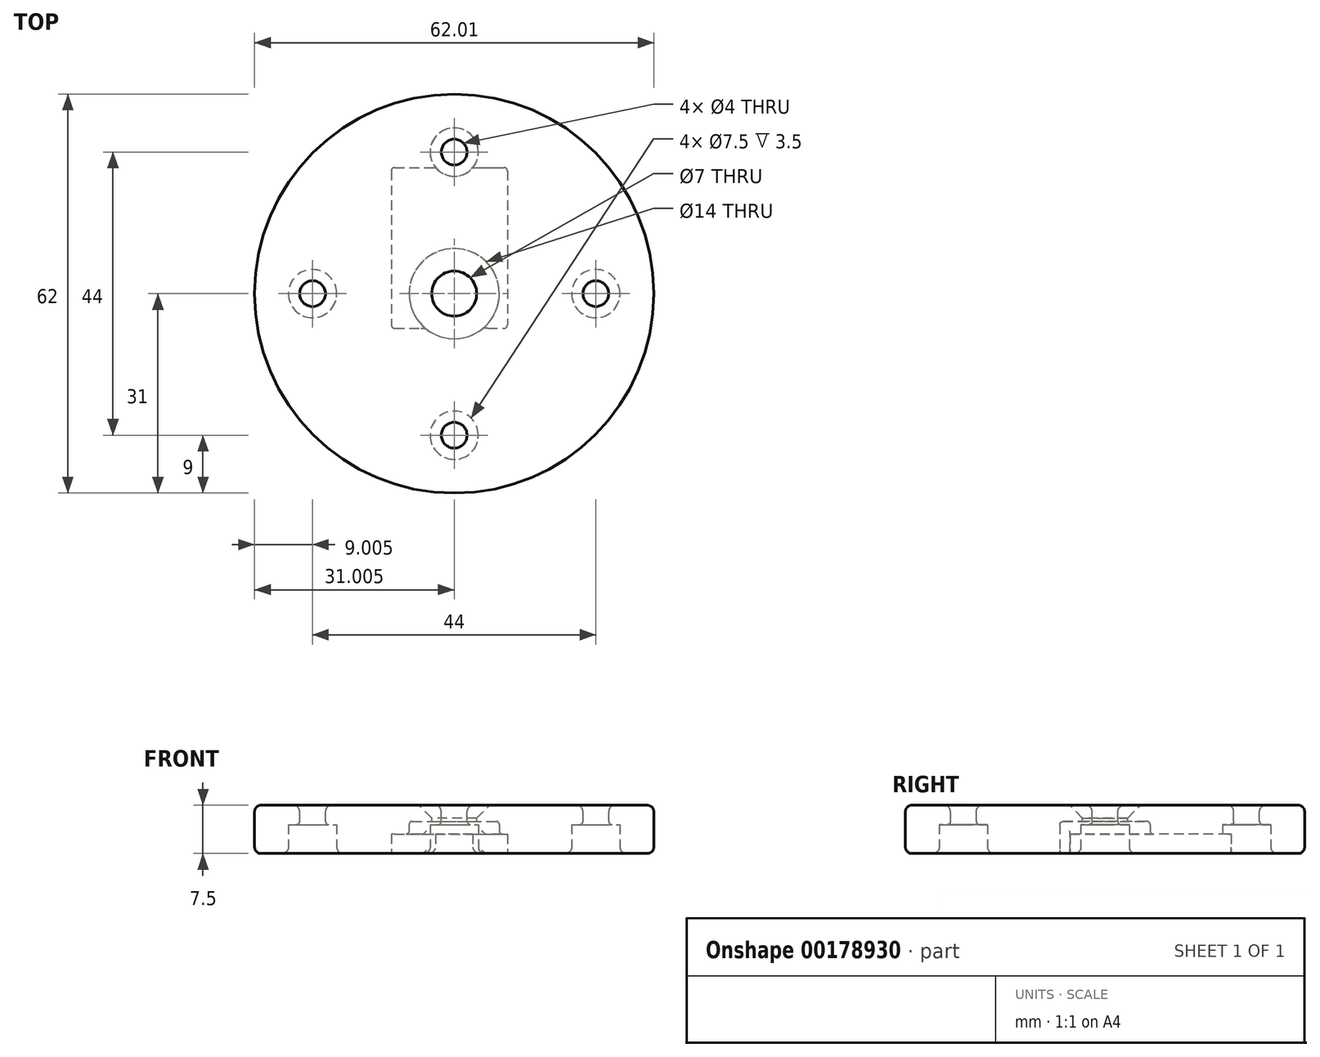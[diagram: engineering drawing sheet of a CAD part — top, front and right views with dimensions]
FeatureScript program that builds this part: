
annotation { "Feature Type Name" : "Feature", "Feature Type Description" : "" }
export const myFeature = defineFeature(function(context is Context, id is Id, definition is map)
    precondition{}
    {
        {
            var Q0;
            Q0=qCreatedBy(makeId("Top.planeOp"),FACE);
            var sketch = newSketch(context, id + "F0", { "sketchPlane" : qUnion([Q0])});
            skLineSegment(sketch, "E0", {"start": v(0, 0) * mm, "end": v(44.88, 0) * mm, "construction": true});
            skLineSegment(sketch, "E1", {"start": v(0, 0) * mm, "end": v(-44.88, 0) * mm, "construction": true});
            skCircle(sketch, "E2", {"center": v(-44.88, 0) * mm, "radius": 3.5 * mm});
            skCircle(sketch, "E3", {"center": v(44.88, 0) * mm, "radius": 3.5 * mm});
            skCircle(sketch, "E4", {"center": v(-44.88, 0) * mm, "radius": 31 * mm});
            skCircle(sketch, "E5", {"center": v(-44.88, 0) * mm, "radius": 22 * mm, "construction": true});
            skPoint(sketch, "E6", {"position": v(-44.88, 22) * mm});
            skPoint(sketch, "E7", {"position": v(-66.87, 0) * mm});
            skPoint(sketch, "E8", {"position": v(-44.88, -22) * mm});
            skPoint(sketch, "E9", {"position": v(-22.88, 0) * mm});
            skCircle(sketch, "E10", {"center": v(-44.88, 22) * mm, "radius": 2 * mm});
            skCircle(sketch, "E11", {"center": v(-66.87, 0) * mm, "radius": 2 * mm});
            skCircle(sketch, "E12", {"center": v(-44.88, -22) * mm, "radius": 2 * mm});
            skCircle(sketch, "E13", {"center": v(-22.88, 0) * mm, "radius": 2 * mm});
            skSolve(sketch);
        }
        {
            var Q0;
            Q0=makeQuery(id+"F0.imprint","IMPRINT",FACE,{"disambiguationData":[TD([[makeQuery(id+"F0.imprint","IMPRINT",EDGE,{"derivedFrom":sQuery(id+"F0.wireOp",EDGE,"E10")}),-1.0]])]});
            var Q1;
            Q1=makeQuery(id+"F0.imprint","IMPRINT",FACE,{"disambiguationData":[TD([[makeQuery(id+"F0.imprint","IMPRINT",EDGE,{"derivedFrom":sQuery(id+"F0.wireOp",EDGE,"E13")}),-1.0]])]});
            extrude(context, id + "F1", {"entities" : qUnion([Q0, Q1]), "oppositeDirection" : true, "depth" : 7.5 * mm});
        }
        {
            var Q0;
            Q0=makeQuery(id+"F1.opExtrude","CAP_FACE",FACE,{"disambiguationData":[OSD([sQuery(id+"F0.wireOp",EDGE,"UtSojWLK-Axtw-wVSr-lVTc-6Qd8189fFZQg"),sQuery(id+"F0.wireOp",EDGE,"E2"),sQuery(id+"F0.wireOp",EDGE,"E3"),sQuery(id+"F0.wireOp",EDGE,"FokHbOu8-fEOc-FsWC-vcUf-28nsGhh90SPb"),sQuery(id+"F0.wireOp",EDGE,"ryVjNOqA-lODm-GvTz-wMqV-SOG7XD1yc1lL"),sQuery(id+"F0.wireOp",EDGE,"E4"),sQuery(id+"F0.wireOp",EDGE,"E10"),sQuery(id+"F0.wireOp",EDGE,"E11"),sQuery(id+"F0.wireOp",EDGE,"E12"),sQuery(id+"F0.wireOp",EDGE,"E13")])],"isStart":false});
            var sketch = newSketch(context, id + "F2", { "sketchPlane" : qUnion([Q0])});
            skCircle(sketch, "E14", {"center": v(-44.88, 22) * mm, "radius": 3.75 * mm});
            skCircle(sketch, "E15", {"center": v(-22.88, 0) * mm, "radius": 3.75 * mm});
            skCircle(sketch, "E16", {"center": v(-44.88, -22) * mm, "radius": 3.75 * mm});
            skCircle(sketch, "E17", {"center": v(-66.87, 0) * mm, "radius": 3.75 * mm});
            skSolve(sketch);
        }
        {
            var Q0;
            Q0=qSketchRegion(id+"F2",true);
            extrude(context, id + "F3", {"entities" : qUnion([Q0]), "operationType" : NewBodyOperationType.REMOVE, "oppositeDirection" : true, "depth" : 4.5 * mm});
        }
        {
            var Q0;
            Q0=makeQuery(id+"F1.opExtrude","CAP_EDGE",EDGE,{"disambiguationData":[OSD([sQuery(id+"F0.wireOp",EDGE,"E2")])],"isStart":true});
            chamfer(context, id + "F4", {"entities" : qUnion([Q0]), "width" : 2 * mm, "tangentPropagation" : true});
        }
        {
            var Q0;
            Q0=makeQuery(id+"FrYEty1sIvLQoTp_1.opExtrude","CAP_FACE",FACE,{"disambiguationData":[OSD([sQuery(id+"F0.wireOp",EDGE,"S2UXTJ5L-PYoN-hTdS-oQlw-xzllwW9uqox5"),sQuery(id+"F0.wireOp",EDGE,"E2")])],"isStart":false});
            var Q1;
            Q1=makeQuery(id+"F1.opExtrude","CAP_FACE",FACE,{"disambiguationData":[OSD([sQuery(id+"F0.wireOp",EDGE,"S2UXTJ5L-PYoN-hTdS-oQlw-xzllwW9uqox5"),sQuery(id+"F0.wireOp",EDGE,"UtSojWLK-Axtw-wVSr-lVTc-6Qd8189fFZQg"),sQuery(id+"F0.wireOp",EDGE,"E2"),sQuery(id+"F0.wireOp",EDGE,"E3"),sQuery(id+"F0.wireOp",EDGE,"FokHbOu8-fEOc-FsWC-vcUf-28nsGhh90SPb"),sQuery(id+"F0.wireOp",EDGE,"ryVjNOqA-lODm-GvTz-wMqV-SOG7XD1yc1lL")])],"isStart":true});
            var Q2;
            Q2=makeQuery(id+"FrYEty1sIvLQoTp_1.opExtrude","CAP_FACE",FACE,{"disambiguationData":[OSD([sQuery(id+"F0.wireOp",EDGE,"UtSojWLK-Axtw-wVSr-lVTc-6Qd8189fFZQg"),sQuery(id+"F0.wireOp",EDGE,"E3")])],"isStart":false});
            var Q3;
            Q3=makeQuery(id+"F1.opExtrude","CAP_FACE",FACE,{"disambiguationData":[OSD([sQuery(id+"F0.wireOp",EDGE,"S2UXTJ5L-PYoN-hTdS-oQlw-xzllwW9uqox5"),sQuery(id+"F0.wireOp",EDGE,"UtSojWLK-Axtw-wVSr-lVTc-6Qd8189fFZQg"),sQuery(id+"F0.wireOp",EDGE,"E2"),sQuery(id+"F0.wireOp",EDGE,"E3"),sQuery(id+"F0.wireOp",EDGE,"FokHbOu8-fEOc-FsWC-vcUf-28nsGhh90SPb"),sQuery(id+"F0.wireOp",EDGE,"ryVjNOqA-lODm-GvTz-wMqV-SOG7XD1yc1lL")])],"isStart":false});
            fillet(context, id + "F5", {"entities" : qUnion([Q0, Q1, Q2, Q3]), "radius" : 1 * mm, "tangentPropagation" : true, "allowEdgeOverflow" : false});
        }
        {
            var Q0;
            Q0=makeQuery(id+"F1.opExtrude","SWEPT_FACE",FACE,{"disambiguationData":[OSD([sQuery(id+"F0.wireOp",EDGE,"E11")])]});
            var Q1;
            Q1=makeQuery(id+"F1.opExtrude","SWEPT_FACE",FACE,{"disambiguationData":[OSD([sQuery(id+"F0.wireOp",EDGE,"E12")])]});
            var Q2;
            Q2=makeQuery(id+"F1.opExtrude","SWEPT_FACE",FACE,{"disambiguationData":[OSD([sQuery(id+"F0.wireOp",EDGE,"E13")])]});
            var Q3;
            Q3=makeQuery(id+"F1.opExtrude","SWEPT_FACE",FACE,{"disambiguationData":[OSD([sQuery(id+"F0.wireOp",EDGE,"E10")])]});
            fillet(context, id + "F6", {"entities" : qUnion([Q0, Q1, Q2, Q3]), "radius" : .5 * mm, "tangentPropagation" : true, "allowEdgeOverflow" : false});
        }
        {
            var Q0;
            Q0=makeQuery(id+"F1.opExtrude","CAP_FACE",FACE,{"disambiguationData":[OSD([sQuery(id+"F0.wireOp",EDGE,"E2"),sQuery(id+"F0.wireOp",EDGE,"E4"),sQuery(id+"F0.wireOp",EDGE,"E10"),sQuery(id+"F0.wireOp",EDGE,"E11"),sQuery(id+"F0.wireOp",EDGE,"E12"),sQuery(id+"F0.wireOp",EDGE,"E13")])],"isStart":false});
            var sketch = newSketch(context, id + "F7", { "sketchPlane" : qUnion([Q0])});
            skLineSegment(sketch, "E18.bottom", {"start": v(-54.62, -19.6) * mm, "end": v(-36.62, -19.6) * mm});
            skLineSegment(sketch, "E18.top", {"start": v(-54.62, 5.4) * mm, "end": v(-36.62, 5.4) * mm});
            skLineSegment(sketch, "E18.left", {"start": v(-54.62, -19.6) * mm, "end": v(-54.62, 5.4) * mm});
            skLineSegment(sketch, "E18.right", {"start": v(-36.62, -19.6) * mm, "end": v(-36.62, 5.4) * mm});
            skSolve(sketch);
        }
        {
            var Q0;
            Q0 = qSketchRegion(id + "F7", true);
            extrude(context, id + "F8", {"entities" : qUnion([Q0]), "operationType" : NewBodyOperationType.REMOVE, "oppositeDirection" : true, "depth" : 3 * mm});
        }
        {
            var Q0;
            Q0=makeQuery(id+"F8.boolean.opBoolean","COPY",FACE,{"derivedFrom":makeQuery(id+"F8.opExtrude","CAP_FACE",FACE,{"disambiguationData":[OSD([sQuery(id+"F7.wireOp",EDGE,"E18.bottom"),sQuery(id+"F7.wireOp",EDGE,"E18.top"),sQuery(id+"F7.wireOp",EDGE,"E18.left"),sQuery(id+"F7.wireOp",EDGE,"E18.right")])],"isStart":false})});
            var sketch = newSketch(context, id + "F9", { "sketchPlane" : qUnion([Q0])});
            skCircle(sketch, "E19", {"center": v(-44.88, 0) * mm, "radius": 7 * mm});
            skSolve(sketch);
        }
        {
            var Q0;
            Q0 = qSketchRegion(id + "F9", true);
            extrude(context, id + "F10", {"entities" : qUnion([Q0]), "operationType" : NewBodyOperationType.REMOVE, "oppositeDirection" : true, "depth" : 2 * mm, "hasSecondDirection" : true, "secondDirectionOppositeDirection" : false, "secondDirectionDepth" : 25 * mm});
        }
        {
            var Q0;
            Q0=makeQuery(id+"F8.boolean.opBoolean","COPY",EDGE,{"derivedFrom":makeQuery(id+"F8.opExtrude","SWEPT_EDGE",EDGE,{"disambiguationData":[OSD([sQuery(id+"F7.wireOp",EDGE,"E18.top"),sQuery(id+"F7.wireOp",EDGE,"E18.left")])]})});
            var Q1;
            Q1=makeQuery(id+"F8.boolean.opBoolean","COPY",EDGE,{"derivedFrom":makeQuery(id+"F8.opExtrude","SWEPT_EDGE",EDGE,{"disambiguationData":[OSD([sQuery(id+"F7.wireOp",EDGE,"E18.top"),sQuery(id+"F7.wireOp",EDGE,"E18.right")])]})});
            var Q2;
            Q2=makeQuery(id+"F8.boolean.opBoolean","COPY",EDGE,{"derivedFrom":makeQuery(id+"F8.opExtrude","SWEPT_EDGE",EDGE,{"disambiguationData":[OSD([sQuery(id+"F7.wireOp",EDGE,"E18.bottom"),sQuery(id+"F7.wireOp",EDGE,"E18.right")])]})});
            var Q3;
            Q3=makeQuery(id+"F8.boolean.opBoolean","COPY",EDGE,{"derivedFrom":makeQuery(id+"F8.opExtrude","SWEPT_EDGE",EDGE,{"disambiguationData":[OSD([sQuery(id+"F7.wireOp",EDGE,"E18.bottom"),sQuery(id+"F7.wireOp",EDGE,"E18.left")])]})});
            var Q4;
            Q4=makeQuery(id+"F8.boolean.opBoolean","INTERSECT",EDGE,{"derivedFrom":[makeQuery(id+"F1.opExtrude","SWEPT_FACE",FACE,{"disambiguationData":[OSD([sQuery(id+"F0.wireOp",EDGE,"E2")])]}),makeQuery(id+"F8.opExtrude","CAP_FACE",FACE,{"disambiguationData":[OSD([sQuery(id+"F7.wireOp",EDGE,"E18.bottom"),sQuery(id+"F7.wireOp",EDGE,"E18.top"),sQuery(id+"F7.wireOp",EDGE,"E18.left"),sQuery(id+"F7.wireOp",EDGE,"E18.right")])],"isStart":false})]});
            var Q5;
            Q5=makeQuery(id+"F8.boolean.opBoolean","COPY",EDGE,{"derivedFrom":makeQuery(id+"F8.opExtrude","CAP_EDGE",EDGE,{"disambiguationData":[OSD([sQuery(id+"F7.wireOp",EDGE,"E18.bottom")])],"isStart":true})});
            var Q6;
            Q6=makeQuery(id+"F10.boolean.opBoolean","COPY",FACE,{"derivedFrom":makeQuery(id+"F10.opExtrude","SWEPT_FACE",FACE,{"disambiguationData":[OSD([sQuery(id+"F9.wireOp",EDGE,"E19")])]})});
            fillet(context, id + "F11", {"entities" : qUnion([Q0, Q1, Q2, Q3, Q4, Q5, Q6]), "radius" : .5 * mm, "tangentPropagation" : true, "allowEdgeOverflow" : false});
        }
    });
